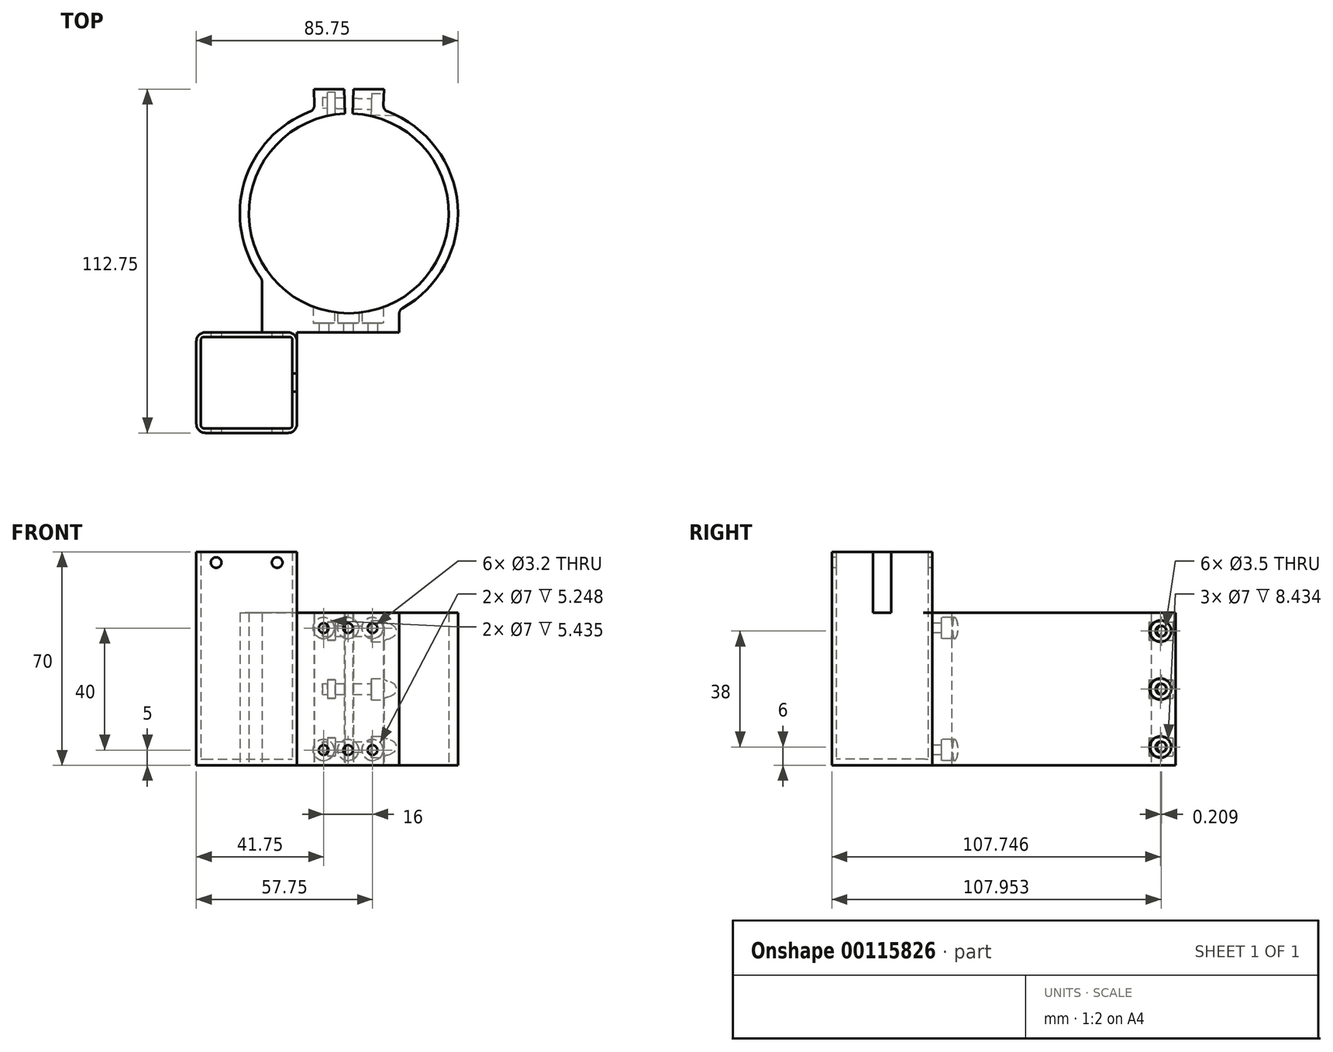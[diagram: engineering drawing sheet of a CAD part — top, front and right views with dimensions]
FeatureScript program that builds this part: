
annotation { "Feature Type Name" : "Feature", "Feature Type Description" : "" }
export const myFeature = defineFeature(function(context is Context, id is Id, definition is map)
    precondition{}
    {
        {
            var Q0;
            Q0=qCreatedBy(makeId("Top.planeOp"),FACE);
            var sketch = newSketch(context, id + "F0", { "sketchPlane" : qUnion([Q0])});
            skArc(sketch, "E0", {"start": v(-1.27, 32.73) * mm, "mid": v(0, -32.75) * mm, "end": v(1.27, 32.73) * mm});
            skArc(sketch, "E1.0", {"start": v(-11.3, 33.92) * mm, "mid": v(-34.15, 10.58) * mm, "end": v(-28.5, -21.58) * mm});
            skLineSegment(sketch, "E2.bottom", {"start": v(1.5, 40.75) * mm, "end": v(11.5, 40.75) * mm});
            skLineSegment(sketch, "E2.left", {"start": v(1.5, 40.75) * mm, "end": v(1.27, 32.73) * mm});
            skLineSegment(sketch, "E2.right", {"start": v(11.5, 40.75) * mm, "end": v(11.3, 33.92) * mm});
            skLineSegment(sketch, "E3.MirrorCS", {"start": v(-1.5, 40.75) * mm, "end": v(-11.5, 40.75) * mm});
            skLineSegment(sketch, "E4.MirrorCS", {"start": v(-1.5, 40.75) * mm, "end": v(-1.27, 32.73) * mm});
            skLineSegment(sketch, "E5.MirrorCS", {"start": v(-11.5, 40.75) * mm, "end": v(-11.3, 33.92) * mm});
            skPoint(sketch, "E6.orphan", {"position": v(-11.27, 32.75) * mm});
            skLineSegment(sketch, "E7.trimOffspring", {"start": v(-11.27, 32.75) * mm, "end": v(-29.08, 32.75) * mm, "construction": true});
            skPoint(sketch, "E8.orphan", {"position": v(11.27, 32.75) * mm});
            skPoint(sketch, "E9.orphan", {"position": v(-1.27, 32.75) * mm});
            skPoint(sketch, "E10.orphan", {"position": v(1.27, 32.75) * mm});
            skPoint(sketch, "E11.orphan", {"position": v(0, 32.75) * mm});
            skLineSegment(sketch, "E12.top", {"start": v(-16.5, -39) * mm, "end": v(16.5, -39) * mm});
            skLineSegment(sketch, "E12.right", {"start": v(16.5, -31.71) * mm, "end": v(16.5, -39) * mm});
            skPoint(sketch, "E13", {"position": v(0, -31.71) * mm});
            skArc(sketch, "E14.trimOffspring", {"start": v(16.5, -31.71) * mm, "mid": v(35.64, 2.82) * mm, "end": v(11.3, 33.92) * mm});
            skLineSegment(sketch, "E15.bottom", {"start": v(-50, -39) * mm, "end": v(-17, -39) * mm});
            skLineSegment(sketch, "E15.top", {"start": v(-50, -72) * mm, "end": v(-17, -72) * mm});
            skLineSegment(sketch, "E15.left", {"start": v(-50, -39) * mm, "end": v(-50, -72) * mm});
            skLineSegment(sketch, "E15.right", {"start": v(-17, -39) * mm, "end": v(-17, -72) * mm});
            skLineSegment(sketch, "E16.bottom", {"start": v(-16.5, -39) * mm, "end": v(-17, -39) * mm});
            skLineSegment(sketch, "E16.right", {"start": v(-28.5, -39) * mm, "end": v(-28.5, -21.58) * mm});
            skLineSegment(sketch, "E17.bottom", {"start": v(-48.5, -40.5) * mm, "end": v(-18.5, -40.5) * mm});
            skLineSegment(sketch, "E17.top", {"start": v(-48.5, -70.5) * mm, "end": v(-18.5, -70.5) * mm});
            skLineSegment(sketch, "E17.left", {"start": v(-48.5, -40.5) * mm, "end": v(-48.5, -70.5) * mm});
            skLineSegment(sketch, "E17.right", {"start": v(-18.5, -40.5) * mm, "end": v(-18.5, -70.5) * mm});
            skSolve(sketch);
        }
        {
            var Q0;
            Q0 = qSketchRegion(id + "F0", true);
            extrude(context, id + "F1", {"entities" : qUnion([Q0]), "depth" : 50 * mm});
        }
        {
            var Q0;
            Q0=makeQuery(id+"F1.opExtrude","SWEPT_FACE",FACE,{"disambiguationData":[OSD([sQuery(id+"F0.wireOp",EDGE,"E12.top")])]});
            var sketch = newSketch(context, id + "F2", { "sketchPlane" : qUnion([Q0])});
            skCircle(sketch, "E18", {"center": v(-8.25, 45) * mm, "radius": 1.6 * mm});
            skCircle(sketch, "E19", {"center": v(-0.25, 45) * mm, "radius": 1.6 * mm});
            skCircle(sketch, "E20", {"center": v(7.75, 45) * mm, "radius": 1.6 * mm});
            skCircle(sketch, "E21", {"center": v(-8.25, 5) * mm, "radius": 1.6 * mm});
            skCircle(sketch, "E22", {"center": v(-0.25, 5) * mm, "radius": 1.6 * mm});
            skCircle(sketch, "E23", {"center": v(7.75, 5) * mm, "radius": 1.6 * mm});
            skPoint(sketch, "E24", {"position": v(-0.25, 50) * mm});
            skPoint(sketch, "E25", {"position": v(16.5, 25) * mm});
            skLineSegment(sketch, "E26", {"start": v(-0.25, 45) * mm, "end": v(-0.25, 5) * mm, "construction": true});
            skPoint(sketch, "E27", {"position": v(-0.25, 25) * mm});
            skSolve(sketch);
        }
        {
            var Q0;
            Q0 = qSketchRegion(id + "F2", true);
            extrude(context, id + "F3", {"entities" : qUnion([Q0]), "operationType" : NewBodyOperationType.REMOVE, "oppositeDirection" : true, "depth" : 25 * mm});
        }
        {
            var Q0;
            Q0=makeQuery(id+"F1.opExtrude","SWEPT_FACE",FACE,{"disambiguationData":[OSD([sQuery(id+"F0.wireOp",EDGE,"E12.top")])]});
            var sketch = newSketch(context, id + "F4", { "sketchPlane" : qUnion([Q0])});
            skCircle(sketch, "E28", {"center": v(-8.25, 45) * mm, "radius": 3.5 * mm});
            skCircle(sketch, "E29", {"center": v(-0.25, 45) * mm, "radius": 3.5 * mm});
            skCircle(sketch, "E30", {"center": v(7.75, 45) * mm, "radius": 3.5 * mm});
            skCircle(sketch, "E31", {"center": v(-8.25, 5) * mm, "radius": 3.5 * mm});
            skCircle(sketch, "E32", {"center": v(-0.25, 5) * mm, "radius": 3.5 * mm});
            skCircle(sketch, "E33", {"center": v(7.75, 5) * mm, "radius": 3.5 * mm});
            skSolve(sketch);
        }
        {
            var Q0;
            Q0 = qSketchRegion(id + "F4", true);
            extrude(context, id + "F5", {"entities" : qUnion([Q0]), "operationType" : NewBodyOperationType.REMOVE, "oppositeDirection" : true, "depth" : 25 * mm, "hasSecondDirection" : true, "secondDirectionOppositeDirection" : true, "secondDirectionDepth" : 3 * mm});
        }
        {
            var Q0;
            Q0=makeQuery(id+"F1.opExtrude","SWEPT_FACE",FACE,{"disambiguationData":[OSD([sQuery(id+"F0.wireOp",EDGE,"E2.right")])]});
            var sketch = newSketch(context, id + "F6", { "sketchPlane" : qUnion([Q0])});
            skCircle(sketch, "E34", {"center": v(36.06, 44) * mm, "radius": 3.5 * mm});
            skCircle(sketch, "E35", {"center": v(36.06, 6) * mm, "radius": 3.5 * mm});
            skCircle(sketch, "E36", {"center": v(36.06, 25) * mm, "radius": 3.5 * mm});
            skLineSegment(sketch, "E37", {"start": v(36.06, 44) * mm, "end": v(36.06, 25) * mm, "construction": true});
            skLineSegment(sketch, "E38", {"start": v(36.06, 25) * mm, "end": v(36.06, 6) * mm, "construction": true});
            skSolve(sketch);
        }
        {
            var Q0;
            {var subQ0=sQuery(id+"F6.wireOp",EDGE,"E34");var subQ1=makeQuery(id+"F1.opExtrude","SWEPT_EDGE",EDGE,{"disambiguationData":[OSD([sQuery(id+"F0.wireOp",EDGE,"E2.right"),sQuery(id+"F0.wireOp",EDGE,"E14.trimOffspring")])]});var subQ2=makeQuery(id+"F6.imprint","INTERSECT",VERTEX,{"disambiguationData":[OD(0.0)],"derivedFrom":[subQ1,subQ0]});Q0=makeQuery(id+"F6.imprint","IMPRINT",FACE,{"disambiguationData":[TD([[makeQuery(id+"F6.imprint","IMPRINT",EDGE,{"disambiguationData":[TD([[subQ2,1.0]])],"derivedFrom":subQ0}),1.0]])]});}
            var Q1;
            {var subQ0=sQuery(id+"F6.wireOp",EDGE,"E36");var subQ1=makeQuery(id+"F1.opExtrude","SWEPT_EDGE",EDGE,{"disambiguationData":[OSD([sQuery(id+"F0.wireOp",EDGE,"E2.right"),sQuery(id+"F0.wireOp",EDGE,"E14.trimOffspring")])]});var subQ2=makeQuery(id+"F6.imprint","INTERSECT",VERTEX,{"disambiguationData":[OD(0.0)],"derivedFrom":[subQ1,subQ0]});Q1=makeQuery(id+"F6.imprint","IMPRINT",FACE,{"disambiguationData":[TD([[makeQuery(id+"F6.imprint","IMPRINT",EDGE,{"disambiguationData":[TD([[subQ2,1.0]])],"derivedFrom":subQ0}),1.0]])]});}
            var Q2;
            {var subQ0=sQuery(id+"F6.wireOp",EDGE,"E35");var subQ1=makeQuery(id+"F1.opExtrude","SWEPT_EDGE",EDGE,{"disambiguationData":[OSD([sQuery(id+"F0.wireOp",EDGE,"E2.right"),sQuery(id+"F0.wireOp",EDGE,"E14.trimOffspring")])]});var subQ2=makeQuery(id+"F6.imprint","INTERSECT",VERTEX,{"disambiguationData":[OD(0.0)],"derivedFrom":[subQ1,subQ0]});Q2=makeQuery(id+"F6.imprint","IMPRINT",FACE,{"disambiguationData":[TD([[makeQuery(id+"F6.imprint","IMPRINT",EDGE,{"disambiguationData":[TD([[subQ2,-1.0]])],"derivedFrom":subQ0}),1.0]])]});}
            var Q3;
            {var subQ0=sQuery(id+"F6.wireOp",EDGE,"E34");var subQ1=makeQuery(id+"F1.opExtrude","SWEPT_EDGE",EDGE,{"disambiguationData":[OSD([sQuery(id+"F0.wireOp",EDGE,"E2.right"),sQuery(id+"F0.wireOp",EDGE,"E14.trimOffspring")])]});var subQ2=makeQuery(id+"F6.imprint","INTERSECT",VERTEX,{"disambiguationData":[OD(0.0)],"derivedFrom":[subQ1,subQ0]});Q3=makeQuery(id+"F6.imprint","IMPRINT",FACE,{"disambiguationData":[TD([[makeQuery(id+"F6.imprint","IMPRINT",EDGE,{"disambiguationData":[TD([[subQ2,-1.0]])],"derivedFrom":subQ0}),1.0]])]});}
            var Q4;
            {var subQ0=sQuery(id+"F6.wireOp",EDGE,"E35");var subQ1=makeQuery(id+"F1.opExtrude","SWEPT_EDGE",EDGE,{"disambiguationData":[OSD([sQuery(id+"F0.wireOp",EDGE,"E2.right"),sQuery(id+"F0.wireOp",EDGE,"E14.trimOffspring")])]});var subQ2=makeQuery(id+"F6.imprint","INTERSECT",VERTEX,{"disambiguationData":[OD(0.0)],"derivedFrom":[subQ1,subQ0]});Q4=makeQuery(id+"F6.imprint","IMPRINT",FACE,{"disambiguationData":[TD([[makeQuery(id+"F6.imprint","IMPRINT",EDGE,{"disambiguationData":[TD([[subQ2,1.0]])],"derivedFrom":subQ0}),1.0]])]});}
            var Q5;
            {var subQ0=sQuery(id+"F6.wireOp",EDGE,"E36");var subQ1=makeQuery(id+"F1.opExtrude","SWEPT_EDGE",EDGE,{"disambiguationData":[OSD([sQuery(id+"F0.wireOp",EDGE,"E2.right"),sQuery(id+"F0.wireOp",EDGE,"E14.trimOffspring")])]});var subQ2=makeQuery(id+"F6.imprint","INTERSECT",VERTEX,{"disambiguationData":[OD(0.0)],"derivedFrom":[subQ1,subQ0]});Q5=makeQuery(id+"F6.imprint","IMPRINT",FACE,{"disambiguationData":[TD([[makeQuery(id+"F6.imprint","IMPRINT",EDGE,{"disambiguationData":[TD([[subQ2,-1.0]])],"derivedFrom":subQ0}),1.0]])]});}
            extrude(context, id + "F7", {"entities" : qUnion([Q0, Q1, Q2, Q3, Q4, Q5]), "operationType" : NewBodyOperationType.REMOVE, "oppositeDirection" : true, "depth" : 4 * mm, "hasSecondDirection" : true, "secondDirectionOppositeDirection" : false, "secondDirectionDepth" : 25 * mm});
        }
        {
            var Q0;
            Q0=makeQuery(id+"F1.opExtrude","SWEPT_FACE",FACE,{"disambiguationData":[OSD([sQuery(id+"F0.wireOp",EDGE,"E2.right")])]});
            var sketch = newSketch(context, id + "F8", { "sketchPlane" : qUnion([Q0])});
            skCircle(sketch, "E39", {"center": v(36.06, 44) * mm, "radius": 1.75 * mm});
            skCircle(sketch, "E40", {"center": v(36.06, 6) * mm, "radius": 1.75 * mm});
            skCircle(sketch, "E41", {"center": v(36.06, 25) * mm, "radius": 1.75 * mm});
            skSolve(sketch);
        }
        {
            var Q0;
            Q0 = qSketchRegion(id + "F8", true);
            extrude(context, id + "F9", {"entities" : qUnion([Q0]), "operationType" : NewBodyOperationType.REMOVE, "oppositeDirection" : true, "depth" : 20 * mm});
        }
        {
            var Q0;
            Q0=makeQuery(id+"F1.opExtrude","SWEPT_FACE",FACE,{"disambiguationData":[OSD([sQuery(id+"F0.wireOp",EDGE,"E3.MirrorCS")])]});
            var sketch = newSketch(context, id + "F10", { "sketchPlane" : qUnion([Q0])});
            skLineSegment(sketch, "E42.bottom", {"start": v(4.5, 47) * mm, "end": v(7, 47) * mm});
            skLineSegment(sketch, "E42.top", {"start": v(4.5, 41) * mm, "end": v(7, 41) * mm});
            skLineSegment(sketch, "E42.left", {"start": v(4.5, 47) * mm, "end": v(4.5, 41) * mm});
            skLineSegment(sketch, "E42.right", {"start": v(7, 47) * mm, "end": v(7, 41) * mm});
            skPoint(sketch, "E43", {"position": v(1.5, 44) * mm});
            skLineSegment(sketch, "E44.0", {"start": v(1.5, 42.25) * mm, "end": v(1.5, 45.75) * mm, "construction": true});
            skPoint(sketch, "E45", {"position": v(4.5, 44) * mm});
            skLineSegment(sketch, "E46.0", {"start": v(1.5, 23.25) * mm, "end": v(1.5, 26.75) * mm});
            skLineSegment(sketch, "E46.1", {"start": v(1.5, 4.25) * mm, "end": v(1.5, 7.75) * mm});
            skLineSegment(sketch, "E47.bottom", {"start": v(4.5, 28) * mm, "end": v(7, 28) * mm});
            skLineSegment(sketch, "E47.top", {"start": v(4.5, 22) * mm, "end": v(7, 22) * mm});
            skLineSegment(sketch, "E47.left", {"start": v(4.5, 28) * mm, "end": v(4.5, 22) * mm});
            skLineSegment(sketch, "E47.right", {"start": v(7, 28) * mm, "end": v(7, 22) * mm});
            skLineSegment(sketch, "E48.bottom", {"start": v(4.5, 9) * mm, "end": v(7, 9) * mm});
            skLineSegment(sketch, "E48.top", {"start": v(4.5, 3) * mm, "end": v(7, 3) * mm});
            skLineSegment(sketch, "E48.left", {"start": v(4.5, 9) * mm, "end": v(4.5, 3) * mm});
            skLineSegment(sketch, "E48.right", {"start": v(7, 9) * mm, "end": v(7, 3) * mm});
            skPoint(sketch, "E49", {"position": v(1.5, 25) * mm});
            skPoint(sketch, "E50", {"position": v(4.5, 25) * mm});
            skPoint(sketch, "E51", {"position": v(1.5, 6) * mm});
            skPoint(sketch, "E52", {"position": v(4.5, 6) * mm});
            skSolve(sketch);
        }
        {
            var Q0;
            Q0 = qSketchRegion(id + "F10", true);
            extrude(context, id + "F11", {"entities" : qUnion([Q0]), "operationType" : NewBodyOperationType.REMOVE, "oppositeDirection" : true, "depth" : 25 * mm, "hasSecondDirection" : true, "secondDirectionOppositeDirection" : true, "secondDirectionDepth" : 1 * mm});
        }
        {
            var Q0;
            Q0=makeQuery(id+"F1.opExtrude","SWEPT_EDGE",EDGE,{"disambiguationData":[OSD([sQuery(id+"F0.wireOp",EDGE,"E12.right"),sQuery(id+"F0.wireOp",EDGE,"E14.trimOffspring")])]});
            var Q1;
            Q1=makeQuery(id+"F1.opExtrude","SWEPT_EDGE",EDGE,{"disambiguationData":[OSD([sQuery(id+"F0.wireOp",EDGE,"E1.0"),sQuery(id+"F0.wireOp",EDGE,"E12.left")])]});
            var Q2;
            {var subQ0=sQuery(id+"F0.wireOp",EDGE,"E14.trimOffspring");var subQ1=sQuery(id+"F0.wireOp",EDGE,"E2.right");Q2=makeQuery(id+"F7.boolean.opBoolean","SPLIT",EDGE,{"disambiguationData":[TD([makeQuery(id+"F1.opExtrude","CAP_FACE",FACE,{"disambiguationData":[OSD([sQuery(id+"F0.wireOp",EDGE,"E0"),sQuery(id+"F0.wireOp",EDGE,"E1.0"),sQuery(id+"F0.wireOp",EDGE,"E2.bottom"),sQuery(id+"F0.wireOp",EDGE,"E2.left"),subQ1,sQuery(id+"F0.wireOp",EDGE,"E3.MirrorCS"),sQuery(id+"F0.wireOp",EDGE,"E4.MirrorCS"),sQuery(id+"F0.wireOp",EDGE,"E5.MirrorCS"),sQuery(id+"F0.wireOp",EDGE,"E12.top"),sQuery(id+"F0.wireOp",EDGE,"E12.left"),sQuery(id+"F0.wireOp",EDGE,"E12.right"),subQ0])],"isStart":false}),makeQuery(id+"F1.opExtrude","SWEPT_FACE",FACE,{"disambiguationData":[OSD([subQ1])]}),makeQuery(id+"F1.opExtrude","SWEPT_FACE",FACE,{"disambiguationData":[OSD([subQ0])]}),makeQuery(id+"F7.opExtrude","SWEPT_FACE",FACE,{"disambiguationData":[OSD([sQuery(id+"F6.wireOp",EDGE,"E34")])]})])],"derivedFrom":makeQuery(id+"F1.opExtrude","SWEPT_EDGE",EDGE,{"disambiguationData":[OSD([subQ1,subQ0])]})});}
            var Q3;
            {var subQ0=sQuery(id+"F0.wireOp",EDGE,"E2.right");var subQ1=sQuery(id+"F0.wireOp",EDGE,"E14.trimOffspring");Q3=makeQuery(id+"F7.boolean.opBoolean","SPLIT",EDGE,{"disambiguationData":[TD([makeQuery(id+"F1.opExtrude","SWEPT_FACE",FACE,{"disambiguationData":[OSD([subQ0])]}),makeQuery(id+"F1.opExtrude","SWEPT_FACE",FACE,{"disambiguationData":[OSD([subQ1])]}),makeQuery(id+"F7.opExtrude","SWEPT_FACE",FACE,{"disambiguationData":[OSD([sQuery(id+"F6.wireOp",EDGE,"E34")])]}),makeQuery(id+"F7.opExtrude","SWEPT_FACE",FACE,{"disambiguationData":[OSD([sQuery(id+"F6.wireOp",EDGE,"E36")])]})])],"derivedFrom":makeQuery(id+"F1.opExtrude","SWEPT_EDGE",EDGE,{"disambiguationData":[OSD([subQ0,subQ1])]})});}
            var Q4;
            {var subQ0=sQuery(id+"F0.wireOp",EDGE,"E2.right");var subQ1=sQuery(id+"F0.wireOp",EDGE,"E14.trimOffspring");Q4=makeQuery(id+"F7.boolean.opBoolean","SPLIT",EDGE,{"disambiguationData":[TD([makeQuery(id+"F1.opExtrude","SWEPT_FACE",FACE,{"disambiguationData":[OSD([subQ0])]}),makeQuery(id+"F1.opExtrude","SWEPT_FACE",FACE,{"disambiguationData":[OSD([subQ1])]}),makeQuery(id+"F7.opExtrude","SWEPT_FACE",FACE,{"disambiguationData":[OSD([sQuery(id+"F6.wireOp",EDGE,"E35")])]}),makeQuery(id+"F7.opExtrude","SWEPT_FACE",FACE,{"disambiguationData":[OSD([sQuery(id+"F6.wireOp",EDGE,"E36")])]})])],"derivedFrom":makeQuery(id+"F1.opExtrude","SWEPT_EDGE",EDGE,{"disambiguationData":[OSD([subQ0,subQ1])]})});}
            var Q5;
            {var subQ0=sQuery(id+"F0.wireOp",EDGE,"E14.trimOffspring");var subQ1=sQuery(id+"F0.wireOp",EDGE,"E2.right");Q5=makeQuery(id+"F7.boolean.opBoolean","SPLIT",EDGE,{"disambiguationData":[TD([makeQuery(id+"F1.opExtrude","CAP_FACE",FACE,{"disambiguationData":[OSD([sQuery(id+"F0.wireOp",EDGE,"E0"),sQuery(id+"F0.wireOp",EDGE,"E1.0"),sQuery(id+"F0.wireOp",EDGE,"E2.bottom"),sQuery(id+"F0.wireOp",EDGE,"E2.left"),subQ1,sQuery(id+"F0.wireOp",EDGE,"E3.MirrorCS"),sQuery(id+"F0.wireOp",EDGE,"E4.MirrorCS"),sQuery(id+"F0.wireOp",EDGE,"E5.MirrorCS"),sQuery(id+"F0.wireOp",EDGE,"E12.top"),sQuery(id+"F0.wireOp",EDGE,"E12.left"),sQuery(id+"F0.wireOp",EDGE,"E12.right"),subQ0])],"isStart":true}),makeQuery(id+"F1.opExtrude","SWEPT_FACE",FACE,{"disambiguationData":[OSD([subQ1])]}),makeQuery(id+"F1.opExtrude","SWEPT_FACE",FACE,{"disambiguationData":[OSD([subQ0])]}),makeQuery(id+"F7.opExtrude","SWEPT_FACE",FACE,{"disambiguationData":[OSD([sQuery(id+"F6.wireOp",EDGE,"E35")])]})])],"derivedFrom":makeQuery(id+"F1.opExtrude","SWEPT_EDGE",EDGE,{"disambiguationData":[OSD([subQ1,subQ0])]})});}
            var Q6;
            Q6=makeQuery(id+"F1.opExtrude","SWEPT_EDGE",EDGE,{"disambiguationData":[OSD([sQuery(id+"F0.wireOp",EDGE,"E1.0"),sQuery(id+"F0.wireOp",EDGE,"E5.MirrorCS")])]});
            fillet(context, id + "F12", {"entities" : qUnion([Q0, Q1, Q2, Q3, Q4, Q5, Q6]), "radius" : 2 * mm, "tangentPropagation" : true, "allowEdgeOverflow" : false});
        }
        {
            var Q0;
            Q0=qCreatedBy(makeId("Top.planeOp"),FACE);
            var sketch = newSketch(context, id + "F13", { "sketchPlane" : qUnion([Q0])});
            skLineSegment(sketch, "E53.0", {"start": v(-48.5, -40.5) * mm, "end": v(-48.5, -70.5) * mm});
            skLineSegment(sketch, "E53.1", {"start": v(-48.5, -40.5) * mm, "end": v(-18.5, -40.5) * mm});
            skLineSegment(sketch, "E53.2", {"start": v(-18.5, -40.5) * mm, "end": v(-18.5, -70.5) * mm});
            skLineSegment(sketch, "E53.3", {"start": v(-48.5, -70.5) * mm, "end": v(-18.5, -70.5) * mm});
            skSolve(sketch);
        }
        {
            var Q0;
            Q0 = qSketchRegion(id + "F13", true);
            extrude(context, id + "F14", {"entities" : qUnion([Q0]), "operationType" : NewBodyOperationType.ADD, "depth" : 2 * mm});
        }
        {
            var Q0;
            Q0=makeQuery(id+"F1.opExtrude","CAP_FACE",FACE,{"disambiguationData":[OSD([sQuery(id+"F0.wireOp",EDGE,"E0"),sQuery(id+"F0.wireOp",EDGE,"E1.0"),sQuery(id+"F0.wireOp",EDGE,"E2.bottom"),sQuery(id+"F0.wireOp",EDGE,"E2.left"),sQuery(id+"F0.wireOp",EDGE,"E2.right"),sQuery(id+"F0.wireOp",EDGE,"E3.MirrorCS"),sQuery(id+"F0.wireOp",EDGE,"E4.MirrorCS"),sQuery(id+"F0.wireOp",EDGE,"E5.MirrorCS"),sQuery(id+"F0.wireOp",EDGE,"E12.top"),sQuery(id+"F0.wireOp",EDGE,"E12.right"),sQuery(id+"F0.wireOp",EDGE,"E14.trimOffspring"),sQuery(id+"F0.wireOp",EDGE,"E15.bottom"),sQuery(id+"F0.wireOp",EDGE,"E15.top"),sQuery(id+"F0.wireOp",EDGE,"E15.left"),sQuery(id+"F0.wireOp",EDGE,"E15.right"),sQuery(id+"F0.wireOp",EDGE,"E16.bottom"),sQuery(id+"F0.wireOp",EDGE,"E16.right"),sQuery(id+"F0.wireOp",EDGE,"E17.bottom"),sQuery(id+"F0.wireOp",EDGE,"E17.top"),sQuery(id+"F0.wireOp",EDGE,"E17.left"),sQuery(id+"F0.wireOp",EDGE,"E17.right")])],"isStart":false});
            var sketch = newSketch(context, id + "F15", { "sketchPlane" : qUnion([Q0])});
            skLineSegment(sketch, "E54.bottom", {"start": v(-50, -39) * mm, "end": v(-17, -39) * mm});
            skLineSegment(sketch, "E54.top", {"start": v(-50, -72) * mm, "end": v(-17, -72) * mm});
            skLineSegment(sketch, "E54.left", {"start": v(-50, -39) * mm, "end": v(-50, -72) * mm});
            skLineSegment(sketch, "E54.right", {"start": v(-17, -39) * mm, "end": v(-17, -72) * mm});
            skLineSegment(sketch, "E55.bottom", {"start": v(-48.5, -40.5) * mm, "end": v(-18.5, -40.5) * mm});
            skLineSegment(sketch, "E55.top", {"start": v(-48.5, -70.5) * mm, "end": v(-18.5, -70.5) * mm});
            skLineSegment(sketch, "E55.left", {"start": v(-48.5, -40.5) * mm, "end": v(-48.5, -70.5) * mm});
            skLineSegment(sketch, "E55.right", {"start": v(-18.5, -40.5) * mm, "end": v(-18.5, -70.5) * mm});
            skSolve(sketch);
        }
        {
            var Q0;
            Q0 = qSketchRegion(id + "F15", true);
            extrude(context, id + "F16", {"entities" : qUnion([Q0]), "operationType" : NewBodyOperationType.ADD, "depth" : 20 * mm});
        }
        {
            var Q0;
            Q0=makeQuery(id+"F16.boolean.opBoolean","MERGE",EDGE,{"derivedFrom":[makeQuery(id+"F1.opExtrude","SWEPT_EDGE",EDGE,{"disambiguationData":[OSD([sQuery(id+"F0.wireOp",EDGE,"E15.top"),sQuery(id+"F0.wireOp",EDGE,"E15.right")])]}),makeQuery(id+"F16.opExtrude","SWEPT_EDGE",EDGE,{"disambiguationData":[OSD([sQuery(id+"F15.wireOp",EDGE,"E54.top"),sQuery(id+"F15.wireOp",EDGE,"E54.right")])]})]});
            var Q1;
            Q1=makeQuery(id+"F16.boolean.opBoolean","MERGE",EDGE,{"derivedFrom":[makeQuery(id+"F1.opExtrude","SWEPT_EDGE",EDGE,{"disambiguationData":[OSD([sQuery(id+"F0.wireOp",EDGE,"E15.top"),sQuery(id+"F0.wireOp",EDGE,"E15.left")])]}),makeQuery(id+"F16.opExtrude","SWEPT_EDGE",EDGE,{"disambiguationData":[OSD([sQuery(id+"F15.wireOp",EDGE,"E54.top"),sQuery(id+"F15.wireOp",EDGE,"E54.left")])]})]});
            var Q2;
            Q2=makeQuery(id+"F16.boolean.opBoolean","MERGE",EDGE,{"derivedFrom":[makeQuery(id+"F1.opExtrude","SWEPT_EDGE",EDGE,{"disambiguationData":[OSD([sQuery(id+"F0.wireOp",EDGE,"E15.bottom"),sQuery(id+"F0.wireOp",EDGE,"E15.left")])]}),makeQuery(id+"F16.opExtrude","SWEPT_EDGE",EDGE,{"disambiguationData":[OSD([sQuery(id+"F15.wireOp",EDGE,"E54.bottom"),sQuery(id+"F15.wireOp",EDGE,"E54.left")])]})]});
            var Q3;
            Q3=makeQuery(id+"F16.opExtrude","SWEPT_EDGE",EDGE,{"disambiguationData":[OSD([sQuery(id+"F0.wireOp",EDGE,"E12.top"),sQuery(id+"F0.wireOp",EDGE,"E16.bottom"),sQuery(id+"F15.wireOp",EDGE,"E54.bottom"),sQuery(id+"F15.wireOp",EDGE,"E54.right")])]});
            fillet(context, id + "F17", {"entities" : qUnion([Q0, Q1, Q2, Q3]), "radius" : 3 * mm, "tangentPropagation" : true, "allowEdgeOverflow" : false});
        }
        {
            var Q0;
            Q0=makeQuery(id+"F16.boolean.opBoolean","MERGE",EDGE,{"derivedFrom":[makeQuery(id+"F1.opExtrude","SWEPT_EDGE",EDGE,{"disambiguationData":[OSD([sQuery(id+"F0.wireOp",EDGE,"E17.bottom"),sQuery(id+"F0.wireOp",EDGE,"E17.left")])]}),makeQuery(id+"F16.opExtrude","SWEPT_EDGE",EDGE,{"disambiguationData":[OSD([sQuery(id+"F15.wireOp",EDGE,"E55.bottom"),sQuery(id+"F15.wireOp",EDGE,"E55.left")])]})]});
            var Q1;
            Q1=makeQuery(id+"F16.boolean.opBoolean","MERGE",EDGE,{"derivedFrom":[makeQuery(id+"F1.opExtrude","SWEPT_EDGE",EDGE,{"disambiguationData":[OSD([sQuery(id+"F0.wireOp",EDGE,"E17.bottom"),sQuery(id+"F0.wireOp",EDGE,"E17.right")])]}),makeQuery(id+"F16.opExtrude","SWEPT_EDGE",EDGE,{"disambiguationData":[OSD([sQuery(id+"F15.wireOp",EDGE,"E55.bottom"),sQuery(id+"F15.wireOp",EDGE,"E55.right")])]})]});
            var Q2;
            Q2=makeQuery(id+"F16.boolean.opBoolean","MERGE",EDGE,{"derivedFrom":[makeQuery(id+"F1.opExtrude","SWEPT_EDGE",EDGE,{"disambiguationData":[OSD([sQuery(id+"F0.wireOp",EDGE,"E17.top"),sQuery(id+"F0.wireOp",EDGE,"E17.right")])]}),makeQuery(id+"F16.opExtrude","SWEPT_EDGE",EDGE,{"disambiguationData":[OSD([sQuery(id+"F15.wireOp",EDGE,"E55.top"),sQuery(id+"F15.wireOp",EDGE,"E55.right")])]})]});
            var Q3;
            Q3=makeQuery(id+"F16.boolean.opBoolean","MERGE",EDGE,{"derivedFrom":[makeQuery(id+"F1.opExtrude","SWEPT_EDGE",EDGE,{"disambiguationData":[OSD([sQuery(id+"F0.wireOp",EDGE,"E17.top"),sQuery(id+"F0.wireOp",EDGE,"E17.left")])]}),makeQuery(id+"F16.opExtrude","SWEPT_EDGE",EDGE,{"disambiguationData":[OSD([sQuery(id+"F15.wireOp",EDGE,"E55.top"),sQuery(id+"F15.wireOp",EDGE,"E55.left")])]})]});
            fillet(context, id + "F18", {"entities" : qUnion([Q0, Q1, Q2, Q3]), "radius" : 1 * mm, "tangentPropagation" : true, "allowEdgeOverflow" : false});
        }
        {
            var Q0;
            Q0=makeQuery(id+"F16.boolean.opBoolean","MERGE",FACE,{"derivedFrom":[makeQuery(id+"F1.opExtrude","SWEPT_FACE",FACE,{"disambiguationData":[OSD([sQuery(id+"F0.wireOp",EDGE,"E15.top")])]}),makeQuery(id+"F16.opExtrude","SWEPT_FACE",FACE,{"disambiguationData":[OSD([sQuery(id+"F15.wireOp",EDGE,"E54.top")])]})]});
            var sketch = newSketch(context, id + "F19", { "sketchPlane" : qUnion([Q0])});
            skCircle(sketch, "E56", {"center": v(-43.5, 66.5) * mm, "radius": 1.75 * mm});
            skCircle(sketch, "E57", {"center": v(-23.5, 66.5) * mm, "radius": 1.75 * mm});
            skSolve(sketch);
        }
        {
            var Q0;
            Q0 = qSketchRegion(id + "F19", true);
            extrude(context, id + "F20", {"entities" : qUnion([Q0]), "operationType" : NewBodyOperationType.REMOVE, "oppositeDirection" : true, "depth" : 40 * mm});
        }
        {
            var Q0;
            Q0=qCreatedBy(makeId("Right.planeOp"),FACE);
            var sketch = newSketch(context, id + "F21", { "sketchPlane" : qUnion([Q0])});
            skLineSegment(sketch, "E58.bottom", {"start": v(-58.5, 70) * mm, "end": v(-52.5, 70) * mm});
            skLineSegment(sketch, "E58.top", {"start": v(-58.5, 50) * mm, "end": v(-52.5, 50) * mm});
            skLineSegment(sketch, "E58.left", {"start": v(-58.5, 70) * mm, "end": v(-58.5, 50) * mm});
            skLineSegment(sketch, "E58.right", {"start": v(-52.5, 70) * mm, "end": v(-52.5, 50) * mm});
            skPoint(sketch, "E59", {"position": v(-55.5, 70) * mm});
            skSolve(sketch);
        }
        {
            var Q0;
            Q0 = qSketchRegion(id + "F21", true);
            extrude(context, id + "F22", {"entities" : qUnion([Q0]), "operationType" : NewBodyOperationType.REMOVE, "oppositeDirection" : true, "depth" : 25 * mm});
        }
    });
